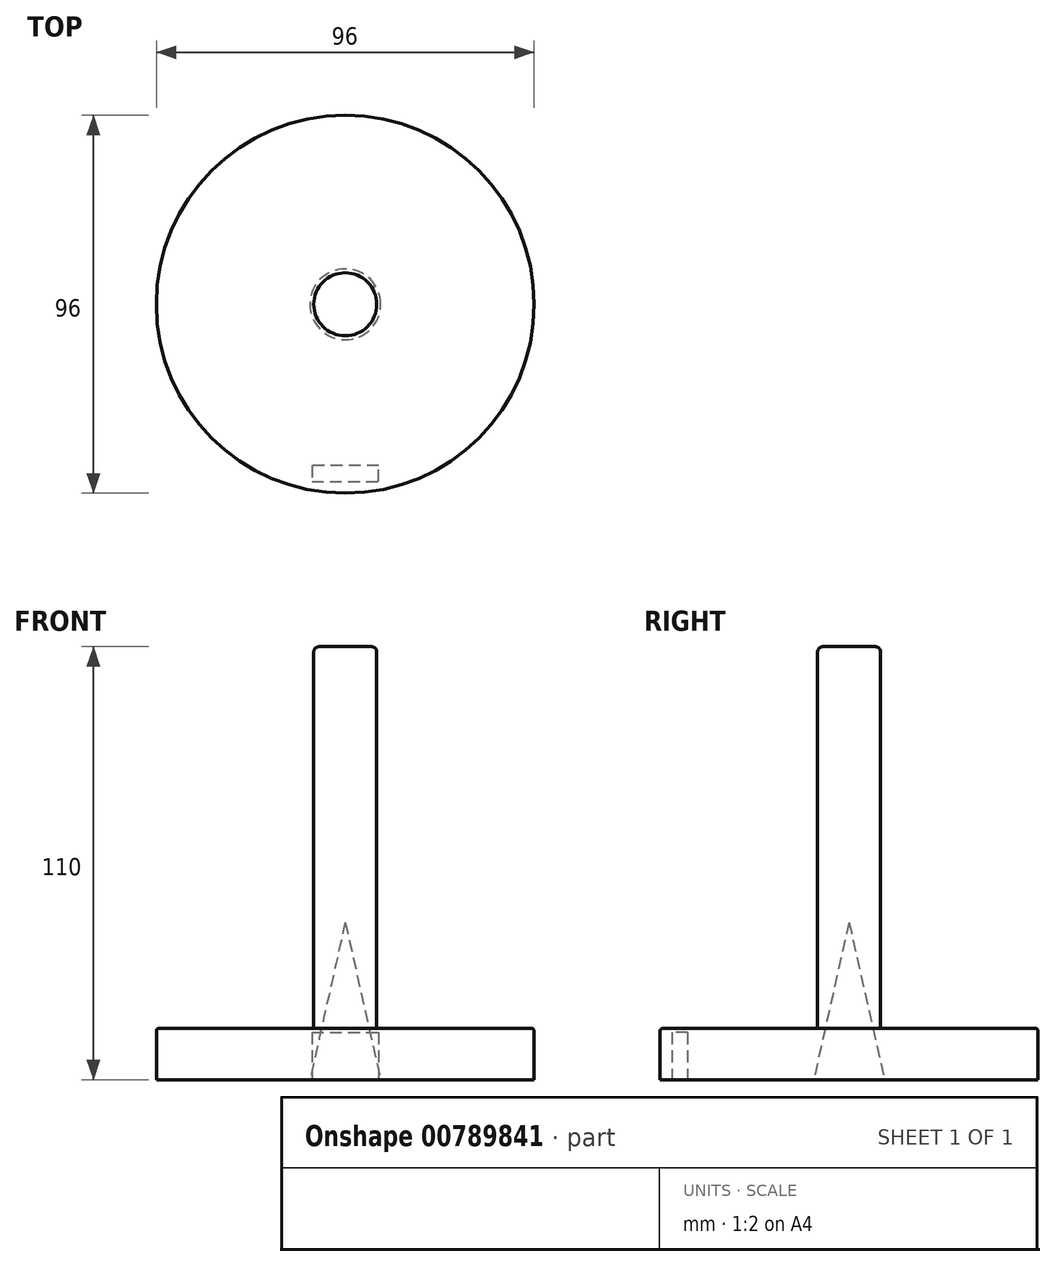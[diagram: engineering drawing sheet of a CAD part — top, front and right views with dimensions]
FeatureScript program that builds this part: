
annotation { "Feature Type Name" : "Feature", "Feature Type Description" : "" }
export const myFeature = defineFeature(function(context is Context, id is Id, definition is map)
    precondition{}
    {
        {
            var Q0;
            Q0=qCreatedBy(makeId("Front.planeOp"),FACE);
            var sketch = newSketch(context, id + "F0", { "sketchPlane" : qUnion([Q0])});
            skLineSegment(sketch, "E0", {"start": v(0, 40) * mm, "end": v(0, 110) * mm});
            skLineSegment(sketch, "E1", {"start": v(0, 110) * mm, "end": v(8, 110) * mm});
            skLineSegment(sketch, "E2", {"start": v(8, 110) * mm, "end": v(8, 13) * mm});
            skLineSegment(sketch, "E3", {"start": v(8, 13) * mm, "end": v(48, 13) * mm});
            skLineSegment(sketch, "E4", {"start": v(48, 13) * mm, "end": v(48, 0) * mm});
            skLineSegment(sketch, "E5", {"start": v(48, 0) * mm, "end": v(9, 0) * mm});
            skPoint(sketch, "E6", {"position": v(0, 40) * mm});
            skLineSegment(sketch, "E7", {"start": v(0, 40) * mm, "end": v(9, 0) * mm});
            skPoint(sketch, "E8.orphan", {"position": v(0, 0) * mm});
            skSolve(sketch);
        }
        {
            var Q0;
            {var subQ0=sQuery(id+"F0.wireOp",EDGE,"E1");Q0=makeQuery(id+"F0.imprint","IMPRINT",FACE,{"disambiguationData":[TD([[makeQuery(id+"F0.imprint","IMPRINT",EDGE,{"derivedFrom":subQ0}),-1.0]])]});}
            var Q1;
            Q1=sQuery(id+"F0.wireOp",EDGE,"E0");
            revolve(context, id + "F1", {"surfaceOperationType" : NewSurfaceOperationType.NEW, "entities" : qUnion([Q0]), "axis" : qUnion([Q1]), "revolveType" : RevolveType.FULL});
        }
        {
            var Q0;
            Q0=makeQuery(id+"F1.opRevolve","SWEPT_FACE",FACE,{"disambiguationData":[OSD([sQuery(id+"F0.wireOp",EDGE,"E5")])]});
            var sketch = newSketch(context, id + "F2", { "sketchPlane" : qUnion([Q0])});
            skLineSegment(sketch, "E9", {"start": v(-8.5, 45) * mm, "end": v(8.5, 45) * mm});
            skLineSegment(sketch, "E10", {"start": v(8.5, 45) * mm, "end": v(8.5, 41) * mm});
            skLineSegment(sketch, "E11", {"start": v(8.5, 41) * mm, "end": v(-8.5, 41) * mm});
            skLineSegment(sketch, "E12", {"start": v(-8.5, 41) * mm, "end": v(-8.5, 45) * mm});
            skLineSegment(sketch, "E13", {"start": v(0, 45) * mm, "end": v(0, 41) * mm, "construction": true});
            skPoint(sketch, "E14", {"position": v(0, 48) * mm});
            skPoint(sketch, "E15", {"position": v(0, 0) * mm});
            skSolve(sketch);
        }
        {
            var Q0;
            Q0=makeQuery(id+"F2.imprint","IMPRINT",FACE,{"disambiguationData":[TD([[makeQuery(id+"F2.imprint","IMPRINT",EDGE,{"derivedFrom":sQuery(id+"F2.wireOp",EDGE,"E9")}),-1.0]])]});
            extrude(context, id + "F3", {"entities" : qUnion([Q0]), "operationType" : NewBodyOperationType.REMOVE, "oppositeDirection" : true, "depth" : 12 * mm, "offsetDistance" : 25 * mm});
        }
        {
            var Q0;
            Q0=makeQuery(id+"F1.opRevolve","SWEPT_EDGE",EDGE,{"disambiguationData":[OSD([sQuery(id+"F0.wireOp",EDGE,"E3"),sQuery(id+"F0.wireOp",EDGE,"E4")])]});
            fillet(context, id + "F4", {"entities" : qUnion([Q0]), "radius" : 0.59 * mm, "tangentPropagation" : true, "allowEdgeOverflow" : false});
        }
        {
            var Q0;
            Q0=makeQuery(id+"F1.opRevolve","SWEPT_EDGE",EDGE,{"disambiguationData":[OSD([sQuery(id+"F0.wireOp",EDGE,"E1"),sQuery(id+"F0.wireOp",EDGE,"E2")])]});
            fillet(context, id + "F5", {"entities" : qUnion([Q0]), "radius" : 1.3 * mm, "tangentPropagation" : true, "allowEdgeOverflow" : false});
        }
        {
            var Q0;
            Q0=makeQuery(id+"F1.opRevolve","SWEPT_FACE",FACE,{"disambiguationData":[OSD([sQuery(id+"F0.wireOp",EDGE,"E3")])]});
            cPlane(context, id + "F6", {"entities" : qUnion([Q0]), "cplaneType" : CPlaneType.OFFSET, "offset" : 27 * mm, "width" : 150 * mm, "height" : 150 * mm});
        }
    });
